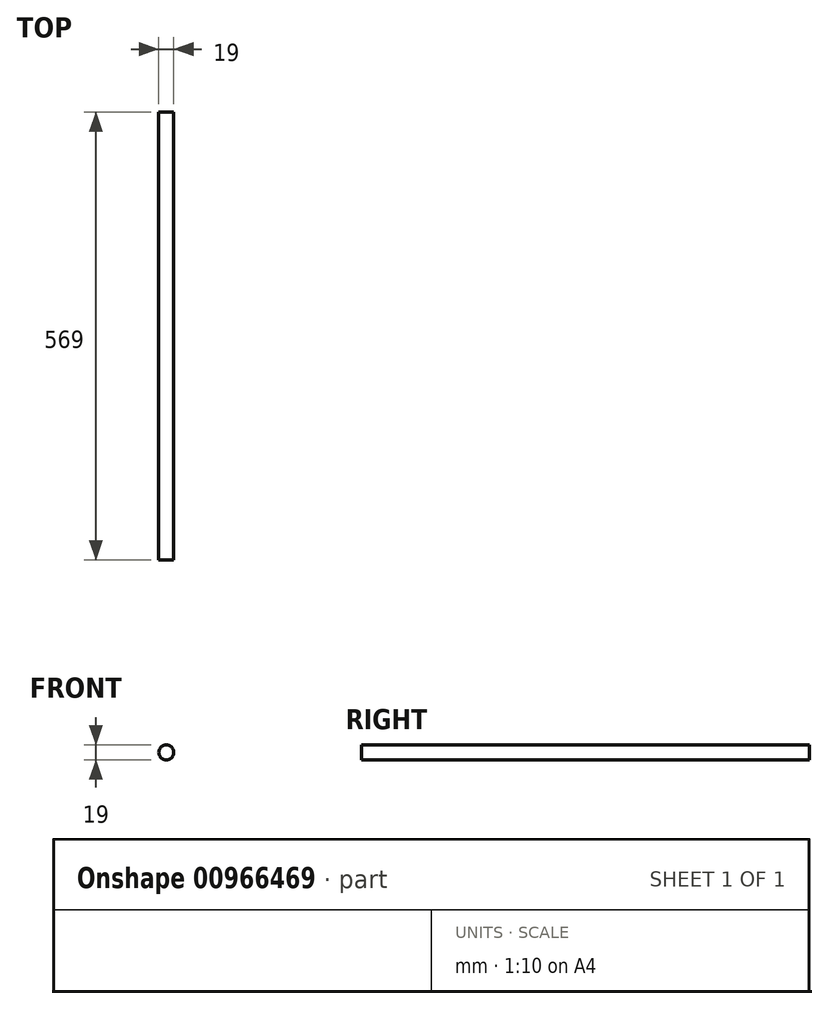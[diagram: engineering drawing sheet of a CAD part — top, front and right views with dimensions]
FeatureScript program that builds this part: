
annotation { "Feature Type Name" : "Feature", "Feature Type Description" : "" }
export const myFeature = defineFeature(function(context is Context, id is Id, definition is map)
    precondition{}
    {
        {
            var Q0;
            Q0=qCreatedBy(makeId("Front.planeOp"),FACE);
            var sketch = newSketch(context, id + "F0", { "sketchPlane" : qUnion([Q0])});
            skCircle(sketch, "E0", {"center": v(0, 0) * mm, "radius": 9.5 * mm});
            skSolve(sketch);
        }
        {
            var Q0;
            Q0=makeQuery(id+"F0.imprint","IMPRINT",FACE,{"disambiguationData":[TD([[makeQuery(id+"F0.imprint","IMPRINT",EDGE,{"derivedFrom":sQuery(id+"F0.wireOp",EDGE,"E0")}),1.0]])]});
            extrude(context, id + "F1", {"entities" : qUnion([Q0]), "depth" : 569 * mm, "offsetDistance" : 25 * mm});
        }
    });
